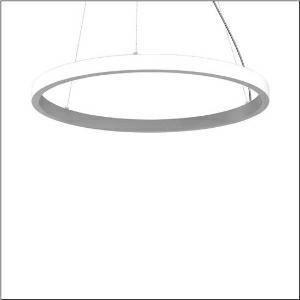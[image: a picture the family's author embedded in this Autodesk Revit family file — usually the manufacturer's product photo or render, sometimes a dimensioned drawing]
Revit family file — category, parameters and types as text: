
# Revit family: silica_r__21_ring-o_5pjbo4d3204a_4430
name_source: partatom
category: Lighting Fixtures
units: mm (PartAtom-declared; Revit-internal decimal feet)

## family parameters
Cut with Voids When Loaded = No
Host = Face
Light Source = No
Part Type = Normal
Room Calculation Point = No
Round Connector Dimension = Use Diameter
Shared = No

## types (1)
- Silica® 21 Ring-O (1 x LED, 9260 lm, 140 W, 4000K)
    Apparent Load = 140 VA
    CIE Flux Codes = 2 16 49 50 100
    Color Rendering = 80
    Color Temperature = 4000K
    Default Elevation = 1800 mm
    Description = Silica® 21 Ring-O, suspended luminaire, of PMMA, frosted, light emission: outer ring side luminous distribution, primary light characteristic: symmetric, installation type: suspended mounting, LED, rated luminous flux: 9.260lm, luminous efficacy: 66lm/W, light colour: 840, colour temperature: 4000K, control gear: DALI 2, with terminal, 5-pole, mains connection: 230V, AC/DC, 0/50..60Hz, rated input power: 140W, housing, of extruded aluminium section, metallic grey (RAL 9006), diameter: 1.480mm, ceiling canopy, metallic grey (RAL 9006), protection rating (lamp compartment): IP40, insulation class (complete): insulation class I (protective earthing), certification: CE, impact resistance: IK02, permissible operating ambient temperature: 0..+35°C, packaging unit: 1 piece
    Height = 48 mm  [stored 0.15748 ft]
    Lamp = 1 x LED
    Lamp Light Flux = 9260 lm
    Lamp Power = 140 W
    Lamp count = 1
    Length = 1480 mm
    Luminous efficacy = 66 lm/W
    Manufacturer = Siteco
    ModVariant = No
    Model = 5PJBO4D3204A
    Mounting Place = Ceiling
    Mounting Type = Pendant
    Number of Poles = 1
    OnlyDefault = Yes
    Power Factor = 1
    Product Name = Silica® 21 Ring-O
    Product group = suspended luminaire
    ProductGroupID = 905
    Protection Class = Protection class I
    Protection Degree = IP 40
    RLX_Detail_Level = 1
    RLX_Emergency_Light_Flux = 0 lm
    RLX_Emergency_Type = 0
    RLX_Emergency_Type_DB = No
    RlxData = <blob elided: 18425 chars, md5=4d2d85b1>
    Socket = socket
    Standby Power = 0 W
    System Light Flux = 9260 lm
    System Power = 140 W
    Type Comments = Product without accessories
    Type Image = l_1251764.jpg
    URL = http://relux.com
    VarID = ---
    Voltage = 0 V
    Weight = 0.00 kg
    Width = 0 mm  [stored 0 ft]

note: [stored X ft] marks values corroborated as IEEE doubles in the binary element streams (Revit-internal decimal feet)

## geometry (parser evidence)
native form markers: Blend x4, Sweep x11
no freeform markers — native parametric forms only
